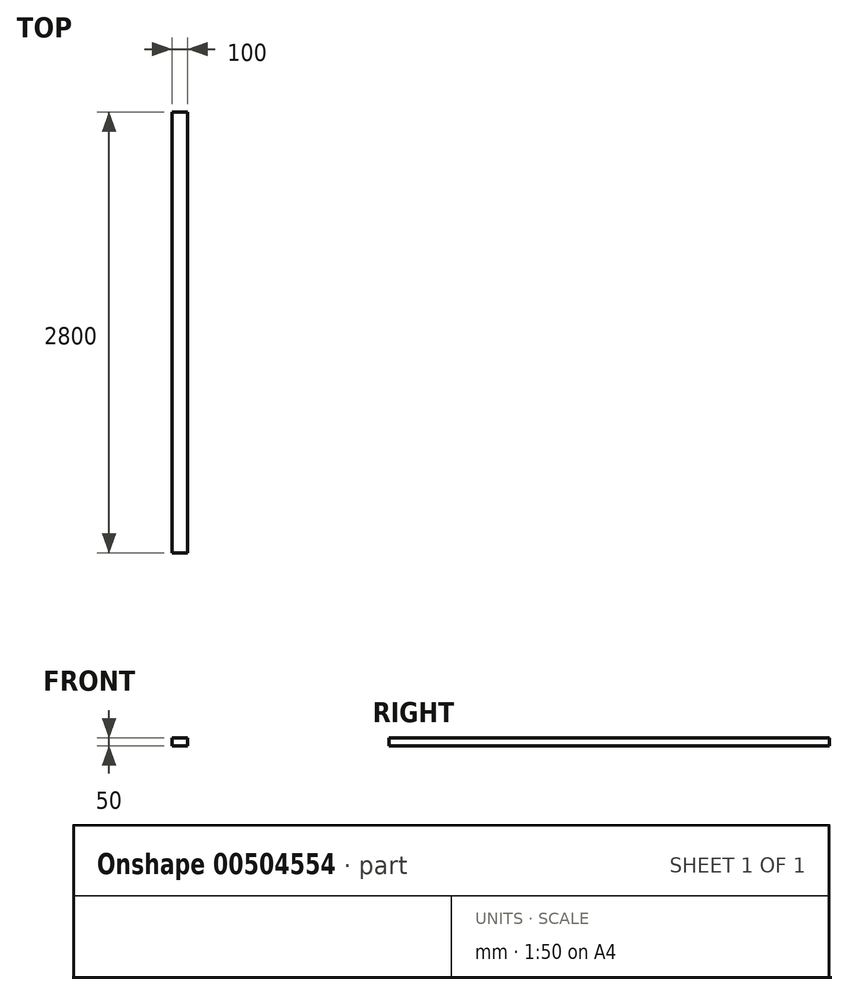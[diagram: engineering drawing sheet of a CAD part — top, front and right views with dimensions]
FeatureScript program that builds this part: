
annotation { "Feature Type Name" : "Feature", "Feature Type Description" : "" }
export const myFeature = defineFeature(function(context is Context, id is Id, definition is map)
    precondition{}
    {
        {
            var Q0;
            Q0=qCreatedBy(makeId("Top.planeOp"),FACE);
            var sketch = newSketch(context, id + "F0", { "sketchPlane" : qUnion([Q0])});
            skLineSegment(sketch, "E0.bottom", {"start": v(1900, -1500) * mm, "end": v(-1900, -1500) * mm});
            skLineSegment(sketch, "E0.top", {"start": v(1900, 1500) * mm, "end": v(-1900, 1500) * mm});
            skLineSegment(sketch, "E0.left", {"start": v(1900, -1500) * mm, "end": v(1900, 1500) * mm});
            skLineSegment(sketch, "E0.right", {"start": v(-1900, -1500) * mm, "end": v(-1900, 1500) * mm});
            skPoint(sketch, "E0.middle", {"position": v(0, 0) * mm});
            skPoint(sketch, "E1", {"position": v(-1900, 1500) * mm});
            skPoint(sketch, "E2", {"position": v(-1900, -1500) * mm});
            skLineSegment(sketch, "E3.bottom", {"start": v(-1900, 1500) * mm, "end": v(-1800, 1500) * mm});
            skLineSegment(sketch, "E3.top", {"start": v(-1900, 1400) * mm, "end": v(-1800, 1400) * mm});
            skLineSegment(sketch, "E3.left", {"start": v(-1900, 1500) * mm, "end": v(-1900, 1400) * mm});
            skLineSegment(sketch, "E3.right", {"start": v(-1800, 1500) * mm, "end": v(-1800, 1400) * mm});
            skLineSegment(sketch, "E4.bottom", {"start": v(-1900, -1500) * mm, "end": v(-1800, -1500) * mm});
            skLineSegment(sketch, "E4.top", {"start": v(-1900, -1400) * mm, "end": v(-1800, -1400) * mm});
            skLineSegment(sketch, "E4.left", {"start": v(-1900, -1500) * mm, "end": v(-1900, -1400) * mm});
            skLineSegment(sketch, "E4.right", {"start": v(-1800, -1500) * mm, "end": v(-1800, -1400) * mm});
            skLineSegment(sketch, "E5.left", {"start": v(-1900, -1400) * mm, "end": v(-1900, 1400) * mm});
            skLineSegment(sketch, "E5.right", {"start": v(-1800, -1400) * mm, "end": v(-1800, 1400) * mm});
            skSolve(sketch);
        }
        {
            var Q0;
            Q0=makeQuery(id+"F0.imprint","IMPRINT",FACE,{"disambiguationData":[TD([[makeQuery(id+"F0.imprint","IMPRINT",EDGE,{"derivedFrom":sQuery(id+"F0.wireOp",EDGE,"E4.bottom")}),1.0]])]});
            var Q1;
            Q1=makeQuery(id+"F0.imprint","IMPRINT",FACE,{"disambiguationData":[TD([[makeQuery(id+"F0.imprint","IMPRINT",EDGE,{"derivedFrom":sQuery(id+"F0.wireOp",EDGE,"E3.bottom")}),-1.0]])]});
            var Q2;
            Q2=makeQuery(id+"F0.imprint","IMPRINT",FACE,{"disambiguationData":[TD([[makeQuery(id+"F0.imprint","IMPRINT",EDGE,{"derivedFrom":sQuery(id+"F0.wireOp",EDGE,"E4.top")}),1.0]])]});
            extrude(context, id + "F1", {"entities" : qUnion([Q0, Q1, Q2]), "depth" : 50 * mm});
        }
    });
